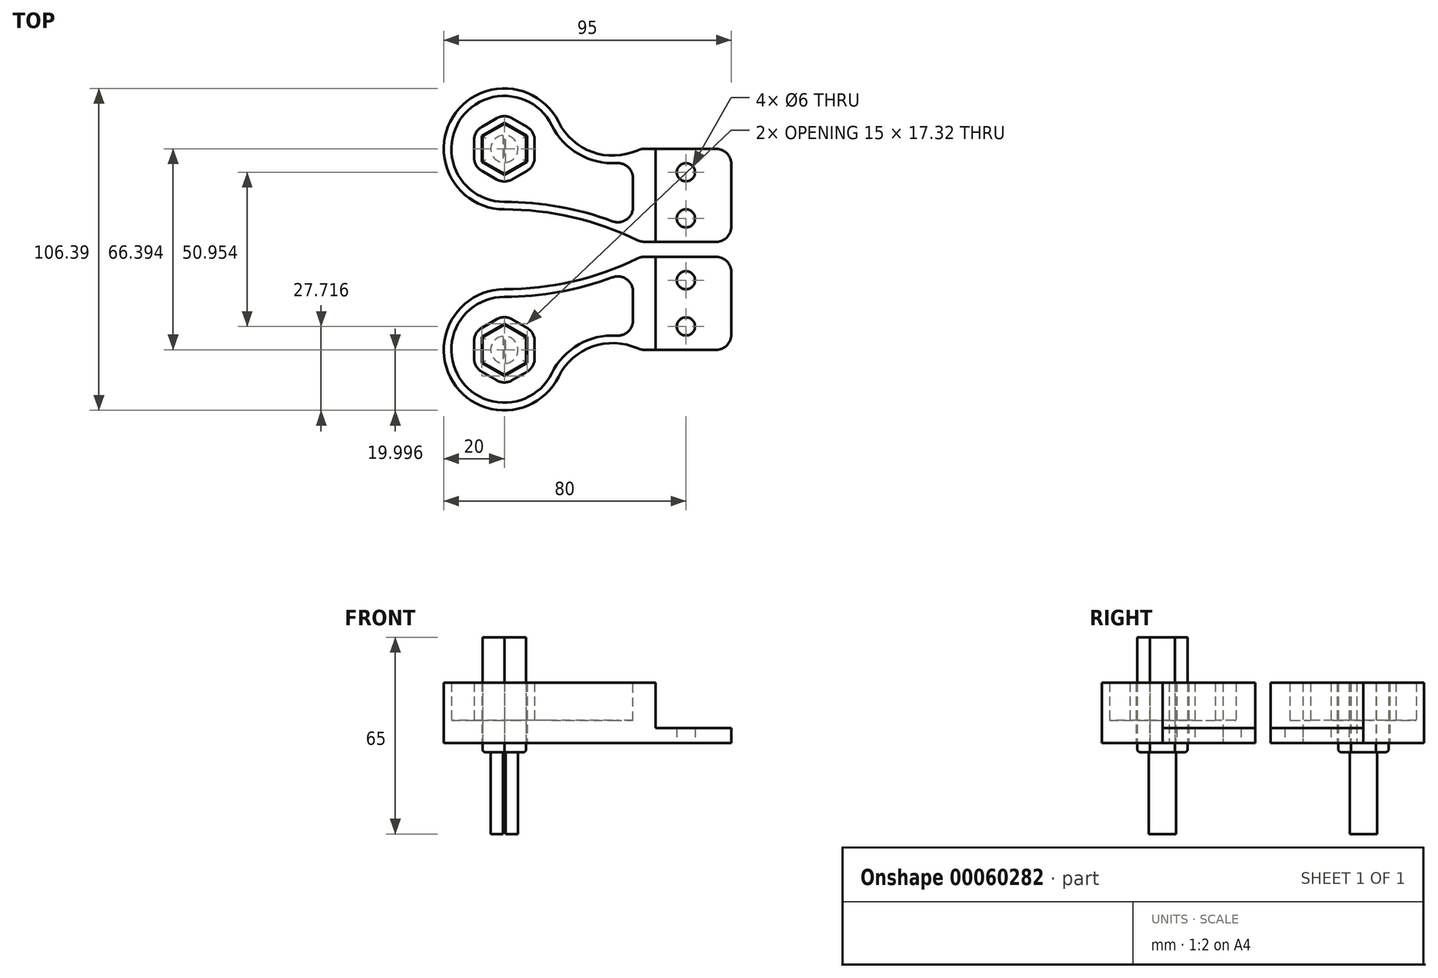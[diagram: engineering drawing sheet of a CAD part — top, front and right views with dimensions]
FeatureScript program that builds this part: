
annotation { "Feature Type Name" : "Feature", "Feature Type Description" : "" }
export const myFeature = defineFeature(function(context is Context, id is Id, definition is map)
    precondition{}
    {
        {
            var Q0;
            Q0=qCreatedBy(makeId("Top.planeOp"),FACE);
            var sketch = newSketch(context, id + "F0", { "sketchPlane" : qUnion([Q0])});
            skCircle(sketch, "E0", {"center": v(0, 0) * mm, "radius": 75 * mm, "construction": true});
            skLineSegment(sketch, "E1", {"start": v(0, 0) * mm, "end": v(75, 0) * mm, "construction": true});
            skCircle(sketch, "E2", {"center": v(0, 0) * mm, "radius": 20 * mm});
            skCircle(sketch, "E3", {"center": v(0, 0) * mm, "radius": 4.5 * mm});
            skCircle(sketch, "E4", {"center": v(0, 0) * mm, "radius": 1.5 * mm});
            skLineSegment(sketch, "E5", {"start": v(0, 0) * mm, "end": v(0, 4.5) * mm, "construction": true});
            skLineSegment(sketch, "E6", {"start": v(-0.5, 4.47) * mm, "end": v(-0.5, 1.41) * mm});
            skLineSegment(sketch, "E7", {"start": v(0.5, -4.47) * mm, "end": v(0.5, -1.41) * mm});
            skLineSegment(sketch, "E8.trimOffspring", {"start": v(-0.5, -1.41) * mm, "end": v(-0.5, -4.47) * mm});
            skLineSegment(sketch, "E9.trimOffspring", {"start": v(0.5, 1.41) * mm, "end": v(0.5, 4.47) * mm});
            skCircle(sketch, "E10.cCircle", {"center": v(0, 0) * mm, "radius": 7.5 * mm, "construction": true});
            skLineSegment(sketch, "E10.0", {"start": v(-7.5, -4.33) * mm, "end": v(-7.5, 4.33) * mm});
            skLineSegment(sketch, "E10.1", {"start": v(-7.5, 4.33) * mm, "end": v(0, 8.66) * mm});
            skLineSegment(sketch, "E10.2", {"start": v(0, 8.66) * mm, "end": v(7.5, 4.33) * mm});
            skLineSegment(sketch, "E10.3", {"start": v(7.5, 4.33) * mm, "end": v(7.5, -4.33) * mm});
            skLineSegment(sketch, "E10.4", {"start": v(7.5, -4.33) * mm, "end": v(0, -8.66) * mm});
            skLineSegment(sketch, "E10.5", {"start": v(0, -8.66) * mm, "end": v(-7.5, -4.33) * mm});
            skPoint(sketch, "E10.0.midPoint", {"position": v(-7.5, 0) * mm});
            skLineSegment(sketch, "E11.bottom", {"start": v(75, 0) * mm, "end": v(45, 0) * mm});
            skLineSegment(sketch, "E11.top", {"start": v(75, -30.7) * mm, "end": v(45, -30.7) * mm});
            skLineSegment(sketch, "E11.left", {"start": v(75, 0) * mm, "end": v(75, -30.7) * mm});
            skLineSegment(sketch, "E11.right", {"start": v(45, 0) * mm, "end": v(45, -30.7) * mm});
            skArc(sketch, "E12", {"start": v(45, -30.7) * mm, "mid": v(23.13, -22.71) * mm, "end": v(0, -20) * mm});
            skArc(sketch, "E13", {"start": v(17.92, 8.89) * mm, "mid": v(29.6, -1.23) * mm, "end": v(45, 0) * mm});
            skLineSegment(sketch, "E14", {"start": v(60, 0) * mm, "end": v(60, -7.72) * mm, "construction": true});
            skLineSegment(sketch, "E15", {"start": v(60, -22.98) * mm, "end": v(60, -30.7) * mm, "construction": true});
            skCircle(sketch, "E16", {"center": v(60, -7.72) * mm, "radius": 3 * mm});
            skCircle(sketch, "E17", {"center": v(60, -22.98) * mm, "radius": 3 * mm});
            skLineSegment(sketch, "E18.0", {"start": v(-7.2, -4.16) * mm, "end": v(-7.2, 4.16) * mm});
            skLineSegment(sketch, "E18.1", {"start": v(0, 8.31) * mm, "end": v(7.2, 4.16) * mm});
            skLineSegment(sketch, "E18.2", {"start": v(7.2, 4.16) * mm, "end": v(7.2, -4.16) * mm});
            skLineSegment(sketch, "E18.3", {"start": v(-7.2, 4.16) * mm, "end": v(0, 8.31) * mm});
            skLineSegment(sketch, "E18.4", {"start": v(7.2, -4.16) * mm, "end": v(0, -8.31) * mm});
            skLineSegment(sketch, "E18.5", {"start": v(0, -8.31) * mm, "end": v(-7.2, -4.16) * mm});
            skLineSegment(sketch, "E19", {"start": v(0.5, 1.41) * mm, "end": v(0.5, -1.41) * mm});
            skLineSegment(sketch, "E20", {"start": v(-0.5, 1.41) * mm, "end": v(-0.5, -1.41) * mm});
            skSolve(sketch);
        }
        {
            var Q0;
            Q0=makeQuery(id+"F0.imprint","IMPRINT",FACE,{"disambiguationData":[TD([[makeQuery(id+"F0.imprint","IMPRINT",EDGE,{"derivedFrom":sQuery(id+"F0.wireOp",EDGE,"E10.0")}),1.0]])]});
            var Q1;
            Q1=makeQuery(id+"F0.imprint","IMPRINT",FACE,{"disambiguationData":[TD([[makeQuery(id+"F0.imprint","IMPRINT",EDGE,{"derivedFrom":sQuery(id+"F0.wireOp",EDGE,"E11.right")}),-1.0]])]});
            var Q2;
            Q2=makeQuery(id+"F0.imprint","IMPRINT",FACE,{"disambiguationData":[TD([[makeQuery(id+"F0.imprint","IMPRINT",EDGE,{"derivedFrom":sQuery(id+"F0.wireOp",EDGE,"E11.bottom")}),1.0]])]});
            extrude(context, id + "F1", {"entities" : qUnion([Q0, Q1, Q2]), "depth" : 5 * mm});
        }
        {
            var Q0;
            Q0=makeQuery(id+"F1.opExtrude","CAP_FACE",FACE,{"disambiguationData":[OSD([sQuery(id+"F0.wireOp",EDGE,"E2"),sQuery(id+"F0.wireOp",EDGE,"E10.0"),sQuery(id+"F0.wireOp",EDGE,"E10.1"),sQuery(id+"F0.wireOp",EDGE,"E10.2"),sQuery(id+"F0.wireOp",EDGE,"E10.3"),sQuery(id+"F0.wireOp",EDGE,"E10.4"),sQuery(id+"F0.wireOp",EDGE,"E10.5"),sQuery(id+"F0.wireOp",EDGE,"E11.bottom"),sQuery(id+"F0.wireOp",EDGE,"E11.top"),sQuery(id+"F0.wireOp",EDGE,"E11.left"),sQuery(id+"F0.wireOp",EDGE,"E12"),sQuery(id+"F0.wireOp",EDGE,"E13")])],"isStart":false});
            var sketch = newSketch(context, id + "F2", { "sketchPlane" : qUnion([Q0])});
            skLineSegment(sketch, "E21.bottom", {"start": v(45, 0) * mm, "end": v(50, 0) * mm});
            skLineSegment(sketch, "E21.top", {"start": v(45, -30.7) * mm, "end": v(50, -30.7) * mm});
            skLineSegment(sketch, "E21.left", {"start": v(45, 0) * mm, "end": v(45, -30.7) * mm});
            skLineSegment(sketch, "E21.right", {"start": v(50, 0) * mm, "end": v(50, -30.7) * mm});
            skSolve(sketch);
        }
        {
            var Q0;
            Q0 = qSketchRegion(id + "F2", true);
            extrude(context, id + "F3", {"entities" : qUnion([Q0]), "operationType" : NewBodyOperationType.ADD, "depth" : 15 * mm});
        }
        {
            var Q0;
            {var subQ0=sQuery(id+"F0.wireOp",EDGE,"E11.bottom");var subQ1=sQuery(id+"F0.wireOp",EDGE,"E10.5");var subQ2=sQuery(id+"F0.wireOp",EDGE,"E10.4");var subQ3=sQuery(id+"F0.wireOp",EDGE,"E10.3");var subQ4=sQuery(id+"F0.wireOp",EDGE,"E2");var subQ5=sQuery(id+"F0.wireOp",EDGE,"E11.top");var subQ6=sQuery(id+"F0.wireOp",EDGE,"E10.0");var subQ7=sQuery(id+"F0.wireOp",EDGE,"E10.1");var subQ8=sQuery(id+"F0.wireOp",EDGE,"E12");var subQ9=sQuery(id+"F0.wireOp",EDGE,"E10.2");var subQ10=sQuery(id+"F0.wireOp",EDGE,"E13");Q0=makeQuery(id+"F3.boolean.opBoolean","SPLIT",FACE,{"disambiguationData":[TD([makeQuery(id+"F1.opExtrude","SWEPT_FACE",FACE,{"disambiguationData":[OSD([subQ4])]})])],"derivedFrom":makeQuery(id+"F1.opExtrude","CAP_FACE",FACE,{"disambiguationData":[OSD([subQ4,subQ6,subQ7,subQ9,subQ3,subQ2,subQ1,subQ0,subQ5,sQuery(id+"F0.wireOp",EDGE,"E11.left"),subQ8,subQ10])],"isStart":false})});}
            extrude(context, id + "F4", {"entities" : qUnion([Q0]), "depth" : 15 * mm});
        }
        {
            var Q0;
            Q0=makeQuery(id+"F4.opExtrude","CAP_FACE",FACE,{"disambiguationData":[OSD([sQuery(id+"F0.wireOp",EDGE,"E2"),sQuery(id+"F0.wireOp",EDGE,"E10.0"),sQuery(id+"F0.wireOp",EDGE,"E10.1"),sQuery(id+"F0.wireOp",EDGE,"E10.2"),sQuery(id+"F0.wireOp",EDGE,"E10.3"),sQuery(id+"F0.wireOp",EDGE,"E10.4"),sQuery(id+"F0.wireOp",EDGE,"E10.5"),sQuery(id+"F0.wireOp",EDGE,"E11.bottom"),sQuery(id+"F0.wireOp",EDGE,"E11.top"),sQuery(id+"F0.wireOp",EDGE,"E11.left"),sQuery(id+"F0.wireOp",EDGE,"E12"),sQuery(id+"F0.wireOp",EDGE,"E13")])],"isStart":false});
            shell(context, id + "F5", {"entities" : qUnion([Q0]), "thickness" : 2.5 * mm});
        }
        {
            var Q0;
            Q0=makeQuery(id+"F1.opExtrude","SWEPT_BODY",BODY,{"disambiguationData":[OSD([sQuery(id+"F0.wireOp",EDGE,"E2"),sQuery(id+"F0.wireOp",EDGE,"E10.0"),sQuery(id+"F0.wireOp",EDGE,"E10.1"),sQuery(id+"F0.wireOp",EDGE,"E10.2"),sQuery(id+"F0.wireOp",EDGE,"E10.3"),sQuery(id+"F0.wireOp",EDGE,"E10.4"),sQuery(id+"F0.wireOp",EDGE,"E10.5"),sQuery(id+"F0.wireOp",EDGE,"E11.bottom"),sQuery(id+"F0.wireOp",EDGE,"E11.top"),sQuery(id+"F0.wireOp",EDGE,"E11.left"),sQuery(id+"F0.wireOp",EDGE,"E12"),sQuery(id+"F0.wireOp",EDGE,"E13")])]});
            var Q1;
            Q1=makeQuery(id+"F4.opExtrude","SWEPT_BODY",BODY,{"disambiguationData":[OSD([sQuery(id+"F0.wireOp",EDGE,"E2"),sQuery(id+"F0.wireOp",EDGE,"E10.0"),sQuery(id+"F0.wireOp",EDGE,"E10.1"),sQuery(id+"F0.wireOp",EDGE,"E10.2"),sQuery(id+"F0.wireOp",EDGE,"E10.3"),sQuery(id+"F0.wireOp",EDGE,"E10.4"),sQuery(id+"F0.wireOp",EDGE,"E10.5"),sQuery(id+"F0.wireOp",EDGE,"E11.bottom"),sQuery(id+"F0.wireOp",EDGE,"E11.top"),sQuery(id+"F0.wireOp",EDGE,"E11.left"),sQuery(id+"F0.wireOp",EDGE,"E12"),sQuery(id+"F0.wireOp",EDGE,"E13")])]});
            booleanBodies(context, id + "F6", {"operationType" : BooleanOperationType.UNION, "tools" : qUnion([Q0, Q1])});
        }
        {
            var Q0;
            Q0=makeQuery(id+"F1.opExtrude","SWEPT_EDGE",EDGE,{"disambiguationData":[OSD([sQuery(id+"F0.wireOp",EDGE,"E11.bottom"),sQuery(id+"F0.wireOp",EDGE,"E11.left")])]});
            var Q1;
            Q1=makeQuery(id+"F1.opExtrude","SWEPT_EDGE",EDGE,{"disambiguationData":[OSD([sQuery(id+"F0.wireOp",EDGE,"E11.top"),sQuery(id+"F0.wireOp",EDGE,"E11.left")])]});
            var Q2;
            {var subQ0=sQuery(id+"F2.wireOp",EDGE,"E21.left");var subQ1=sQuery(id+"F2.wireOp",EDGE,"E21.top");var subQ2=sQuery(id+"F0.wireOp",EDGE,"E12");var subQ3=sQuery(id+"F0.wireOp",EDGE,"E11.right");var subQ4=sQuery(id+"F0.wireOp",EDGE,"E11.top");Q2=makeQuery(id+"F6.opBoolean","MERGE",EDGE,{"derivedFrom":[makeQuery(id+"F1.opExtrude","SWEPT_EDGE",EDGE,{"disambiguationData":[OSD([subQ4,subQ3,subQ2])]}),makeQuery(id+"F3.opExtrude","SWEPT_EDGE",EDGE,{"disambiguationData":[OSD([subQ2,subQ1,subQ0])]}),makeQuery(id+"F4.opExtrude","SWEPT_EDGE",EDGE,{"disambiguationData":[OSD([subQ4,subQ3,subQ2,subQ1,subQ0])]})]});}
            var Q3;
            {var subQ0=sQuery(id+"F2.wireOp",EDGE,"E21.left");var subQ1=sQuery(id+"F2.wireOp",EDGE,"E21.bottom");var subQ2=sQuery(id+"F0.wireOp",EDGE,"E13");var subQ3=sQuery(id+"F0.wireOp",EDGE,"E11.right");var subQ4=sQuery(id+"F0.wireOp",EDGE,"E11.bottom");Q3=makeQuery(id+"F6.opBoolean","MERGE",EDGE,{"derivedFrom":[makeQuery(id+"F1.opExtrude","SWEPT_EDGE",EDGE,{"disambiguationData":[OSD([subQ4,subQ3,subQ2])]}),makeQuery(id+"F3.opExtrude","SWEPT_EDGE",EDGE,{"disambiguationData":[OSD([subQ2,subQ1,subQ0])]}),makeQuery(id+"F4.opExtrude","SWEPT_EDGE",EDGE,{"disambiguationData":[OSD([subQ4,subQ3,subQ2,subQ1,subQ0])]})]});}
            var Q4;
            {var subQ0=sQuery(id+"F0.wireOp",EDGE,"E13");var subQ1=sQuery(id+"F0.wireOp",EDGE,"E2");Q4=makeQuery(id+"F6.opBoolean","MERGE",EDGE,{"derivedFrom":[makeQuery(id+"F1.opExtrude","SWEPT_EDGE",EDGE,{"disambiguationData":[OSD([subQ1,subQ0])]}),makeQuery(id+"F4.opExtrude","SWEPT_EDGE",EDGE,{"disambiguationData":[OSD([subQ1,subQ0])]})]});}
            var Q5;
            {var subQ0=sQuery(id+"F0.wireOp",EDGE,"E12");var subQ1=sQuery(id+"F0.wireOp",EDGE,"E2");Q5=makeQuery(id+"F6.opBoolean","MERGE",EDGE,{"derivedFrom":[makeQuery(id+"F1.opExtrude","SWEPT_EDGE",EDGE,{"disambiguationData":[OSD([subQ1,subQ0])]}),makeQuery(id+"F4.opExtrude","SWEPT_EDGE",EDGE,{"disambiguationData":[OSD([subQ1,subQ0])]})]});}
            var Q6;
            Q6=makeQuery(id+"F5.opShell","OFFSET_EDGE",EDGE,{"disambiguationData":[OSD([sQuery(id+"F0.wireOp",EDGE,"E11.bottom"),sQuery(id+"F0.wireOp",EDGE,"E11.right"),sQuery(id+"F0.wireOp",EDGE,"E13"),sQuery(id+"F2.wireOp",EDGE,"E21.bottom"),sQuery(id+"F2.wireOp",EDGE,"E21.left")])]});
            var Q7;
            Q7=makeQuery(id+"F5.opShell","OFFSET_EDGE",EDGE,{"disambiguationData":[OSD([sQuery(id+"F0.wireOp",EDGE,"E11.top"),sQuery(id+"F0.wireOp",EDGE,"E11.right"),sQuery(id+"F0.wireOp",EDGE,"E12"),sQuery(id+"F2.wireOp",EDGE,"E21.top"),sQuery(id+"F2.wireOp",EDGE,"E21.left")])]});
            var Q8;
            Q8=makeQuery(id+"F5.opShell","OFFSET_EDGE",EDGE,{"disambiguationData":[OSD([sQuery(id+"F0.wireOp",EDGE,"E10.4"),sQuery(id+"F0.wireOp",EDGE,"E10.5")])]});
            var Q9;
            Q9=makeQuery(id+"F5.opShell","OFFSET_EDGE",EDGE,{"disambiguationData":[OSD([sQuery(id+"F0.wireOp",EDGE,"E10.3"),sQuery(id+"F0.wireOp",EDGE,"E10.4")])]});
            var Q10;
            Q10=makeQuery(id+"F5.opShell","OFFSET_EDGE",EDGE,{"disambiguationData":[OSD([sQuery(id+"F0.wireOp",EDGE,"E10.0"),sQuery(id+"F0.wireOp",EDGE,"E10.5")])]});
            var Q11;
            Q11=makeQuery(id+"F5.opShell","OFFSET_EDGE",EDGE,{"disambiguationData":[OSD([sQuery(id+"F0.wireOp",EDGE,"E10.0"),sQuery(id+"F0.wireOp",EDGE,"E10.1")])]});
            var Q12;
            Q12=makeQuery(id+"F5.opShell","OFFSET_EDGE",EDGE,{"disambiguationData":[OSD([sQuery(id+"F0.wireOp",EDGE,"E10.1"),sQuery(id+"F0.wireOp",EDGE,"E10.2")])]});
            var Q13;
            Q13=makeQuery(id+"F5.opShell","OFFSET_EDGE",EDGE,{"disambiguationData":[OSD([sQuery(id+"F0.wireOp",EDGE,"E10.2"),sQuery(id+"F0.wireOp",EDGE,"E10.3")])]});
            fillet(context, id + "F7", {"entities" : qUnion([Q0, Q1, Q2, Q3, Q4, Q5, Q6, Q7, Q8, Q9, Q10, Q11, Q12, Q13]), "radius" : 5 * mm, "tangentPropagation" : true, "allowEdgeOverflow" : false});
        }
        {
            var Q0;
            Q0=makeQuery(id+"F0.imprint","IMPRINT",FACE,{"disambiguationData":[TD([[makeQuery(id+"F0.imprint","IMPRINT",EDGE,{"derivedFrom":sQuery(id+"F0.wireOp",EDGE,"E18.0")}),-1.0]])]});
            var Q1;
            {var subQ0=sQuery(id+"F0.wireOp",EDGE,"E6");Q1=makeQuery(id+"F0.imprint","IMPRINT",FACE,{"disambiguationData":[TD([[makeQuery(id+"F0.imprint","IMPRINT",EDGE,{"derivedFrom":subQ0}),-1.0]])]});}
            var Q2;
            {var subQ0=sQuery(id+"F0.wireOp",EDGE,"E7");Q2=makeQuery(id+"F0.imprint","IMPRINT",FACE,{"disambiguationData":[TD([[makeQuery(id+"F0.imprint","IMPRINT",EDGE,{"derivedFrom":subQ0}),-1.0]])]});}
            var Q3;
            {var subQ0=sQuery(id+"F0.wireOp",EDGE,"E4");var subQ1=makeQuery(id+"F0.imprint","INTERSECT",VERTEX,{"derivedFrom":[subQ0,sQuery(id+"F0.wireOp",EDGE,"E6")]});Q3=makeQuery(id+"F0.imprint","IMPRINT",FACE,{"disambiguationData":[TD([[makeQuery(id+"F0.imprint","IMPRINT",EDGE,{"disambiguationData":[TD([[subQ1,1.0]])],"derivedFrom":subQ0}),1.0]])]});}
            var Q4;
            {var subQ0=sQuery(id+"F0.wireOp",EDGE,"E7");Q4=makeQuery(id+"F0.imprint","IMPRINT",FACE,{"disambiguationData":[TD([[makeQuery(id+"F0.imprint","IMPRINT",EDGE,{"derivedFrom":subQ0}),1.0]])]});}
            var Q5;
            {var subQ0=sQuery(id+"F0.wireOp",EDGE,"E6");Q5=makeQuery(id+"F0.imprint","IMPRINT",FACE,{"disambiguationData":[TD([[makeQuery(id+"F0.imprint","IMPRINT",EDGE,{"derivedFrom":subQ0}),1.0]])]});}
            var Q6;
            {var subQ0=sQuery(id+"F0.wireOp",EDGE,"E19");Q6=makeQuery(id+"F0.imprint","IMPRINT",FACE,{"disambiguationData":[TD([[makeQuery(id+"F0.imprint","IMPRINT",EDGE,{"derivedFrom":subQ0}),1.0]])]});}
            var Q7;
            {var subQ0=sQuery(id+"F0.wireOp",EDGE,"E20");Q7=makeQuery(id+"F0.imprint","IMPRINT",FACE,{"disambiguationData":[TD([[makeQuery(id+"F0.imprint","IMPRINT",EDGE,{"derivedFrom":subQ0}),-1.0]])]});}
            var Q8;
            Q8=makeQuery(id+"F4.opExtrude","CAP_FACE",FACE,{"disambiguationData":[OSD([sQuery(id+"F0.wireOp",EDGE,"E2"),sQuery(id+"F0.wireOp",EDGE,"E10.0"),sQuery(id+"F0.wireOp",EDGE,"E10.1"),sQuery(id+"F0.wireOp",EDGE,"E10.2"),sQuery(id+"F0.wireOp",EDGE,"E10.3"),sQuery(id+"F0.wireOp",EDGE,"E10.4"),sQuery(id+"F0.wireOp",EDGE,"E10.5"),sQuery(id+"F0.wireOp",EDGE,"E11.bottom"),sQuery(id+"F0.wireOp",EDGE,"E11.top"),sQuery(id+"F0.wireOp",EDGE,"E11.left"),sQuery(id+"F0.wireOp",EDGE,"E12"),sQuery(id+"F0.wireOp",EDGE,"E13"),sQuery(id+"F0.wireOp",EDGE,"E16"),sQuery(id+"F0.wireOp",EDGE,"E17")])],"isStart":false});
            extrude(context, id + "F8", {"entities" : qUnion([Q0, Q1, Q2, Q3, Q4, Q5, Q6, Q7]), "endBound" : BoundingType.UP_TO_SURFACE, "endBoundEntityFace" : qUnion([Q8]), "depth" : 25 * mm, "hasSecondDirection" : true, "secondDirectionOppositeDirection" : true, "secondDirectionDepth" : 3 * mm});
        }
        {
            var Q0;
            {var subQ0=sQuery(id+"F0.wireOp",EDGE,"E6");Q0=makeQuery(id+"F0.imprint","IMPRINT",FACE,{"disambiguationData":[TD([[makeQuery(id+"F0.imprint","IMPRINT",EDGE,{"derivedFrom":subQ0}),-1.0]])]});}
            var Q1;
            {var subQ0=sQuery(id+"F0.wireOp",EDGE,"E7");Q1=makeQuery(id+"F0.imprint","IMPRINT",FACE,{"disambiguationData":[TD([[makeQuery(id+"F0.imprint","IMPRINT",EDGE,{"derivedFrom":subQ0}),-1.0]])]});}
            var Q2;
            {var subQ0=sQuery(id+"F0.wireOp",EDGE,"E19");Q2=makeQuery(id+"F0.imprint","IMPRINT",FACE,{"disambiguationData":[TD([[makeQuery(id+"F0.imprint","IMPRINT",EDGE,{"derivedFrom":subQ0}),1.0]])]});}
            var Q3;
            {var subQ0=sQuery(id+"F0.wireOp",EDGE,"E20");Q3=makeQuery(id+"F0.imprint","IMPRINT",FACE,{"disambiguationData":[TD([[makeQuery(id+"F0.imprint","IMPRINT",EDGE,{"derivedFrom":subQ0}),-1.0]])]});}
            extrude(context, id + "F9", {"entities" : qUnion([Q0, Q1, Q2, Q3]), "operationType" : NewBodyOperationType.ADD, "oppositeDirection" : true, "depth" : 30 * mm});
        }
        {
            var Q0;
            Q0=makeQuery(id+"F8.opExtrude","CAP_EDGE",EDGE,{"disambiguationData":[OSD([sQuery(id+"F0.wireOp",EDGE,"E18.3")])],"isStart":true});
            var Q1;
            Q1=makeQuery(id+"F8.opExtrude","CAP_EDGE",EDGE,{"disambiguationData":[OSD([sQuery(id+"F0.wireOp",EDGE,"E18.1")])],"isStart":true});
            var Q2;
            Q2=makeQuery(id+"F8.opExtrude","CAP_EDGE",EDGE,{"disambiguationData":[OSD([sQuery(id+"F0.wireOp",EDGE,"E18.2")])],"isStart":true});
            var Q3;
            Q3=makeQuery(id+"F8.opExtrude","CAP_EDGE",EDGE,{"disambiguationData":[OSD([sQuery(id+"F0.wireOp",EDGE,"E18.4")])],"isStart":true});
            var Q4;
            Q4=makeQuery(id+"F8.opExtrude","CAP_EDGE",EDGE,{"disambiguationData":[OSD([sQuery(id+"F0.wireOp",EDGE,"E18.0")])],"isStart":true});
            var Q5;
            Q5=makeQuery(id+"F8.opExtrude","CAP_EDGE",EDGE,{"disambiguationData":[OSD([sQuery(id+"F0.wireOp",EDGE,"E18.5")])],"isStart":true});
            fillet(context, id + "F10", {"entities" : qUnion([Q0, Q1, Q2, Q3, Q4, Q5]), "radius" : 1 * mm, "tangentPropagation" : true, "allowEdgeOverflow" : false});
        }
        {
            var Q0;
            Q0=makeQuery(id+"F8.opExtrude","SWEPT_BODY",BODY,{"disambiguationData":[OSD([sQuery(id+"F0.wireOp",EDGE,"E18.0"),sQuery(id+"F0.wireOp",EDGE,"E18.1"),sQuery(id+"F0.wireOp",EDGE,"E18.2"),sQuery(id+"F0.wireOp",EDGE,"E18.3"),sQuery(id+"F0.wireOp",EDGE,"E18.4"),sQuery(id+"F0.wireOp",EDGE,"E18.5")])]});
            transform(context, id + "F11", {"entities" : qUnion([Q0]), "transformType" : TransformType.TRANSLATION_3D, "dx" : 0 * mm, "dy" : -59.65 * mm, "dz" : 0 * mm, "makeCopy" : true});
        }
        {
            var Q0;
            Q0=makeQuery(id+"F11.opPattern","COPY",FACE,{"derivedFrom":makeQuery(id+"F8.opExtrude","CAP_FACE",FACE,{"disambiguationData":[OSD([sQuery(id+"F0.wireOp",EDGE,"E18.0"),sQuery(id+"F0.wireOp",EDGE,"E18.1"),sQuery(id+"F0.wireOp",EDGE,"E18.2"),sQuery(id+"F0.wireOp",EDGE,"E18.3"),sQuery(id+"F0.wireOp",EDGE,"E18.4"),sQuery(id+"F0.wireOp",EDGE,"E18.5")])],"isStart":false}),"instanceName":"1"});
            extrude(context, id + "F12", {"entities" : qUnion([Q0]), "operationType" : NewBodyOperationType.ADD, "depth" : 15 * mm});
        }
        {
            var Q0;
            Q0=makeQuery(id+"F1.opExtrude","SWEPT_BODY",BODY,{"disambiguationData":[OSD([sQuery(id+"F0.wireOp",EDGE,"E2"),sQuery(id+"F0.wireOp",EDGE,"E10.0"),sQuery(id+"F0.wireOp",EDGE,"E10.1"),sQuery(id+"F0.wireOp",EDGE,"E10.2"),sQuery(id+"F0.wireOp",EDGE,"E10.3"),sQuery(id+"F0.wireOp",EDGE,"E10.4"),sQuery(id+"F0.wireOp",EDGE,"E10.5"),sQuery(id+"F0.wireOp",EDGE,"E11.bottom"),sQuery(id+"F0.wireOp",EDGE,"E11.top"),sQuery(id+"F0.wireOp",EDGE,"E11.left"),sQuery(id+"F0.wireOp",EDGE,"E12"),sQuery(id+"F0.wireOp",EDGE,"E13"),sQuery(id+"F0.wireOp",EDGE,"E16"),sQuery(id+"F0.wireOp",EDGE,"E17")])]});
            var Q1;
            Q1=makeQuery(id+"F3.boolean.opBoolean","MERGE",FACE,{"derivedFrom":[makeQuery(id+"F1.opExtrude","SWEPT_FACE",FACE,{"disambiguationData":[OSD([sQuery(id+"F0.wireOp",EDGE,"E11.top")])]}),makeQuery(id+"F3.opExtrude","SWEPT_FACE",FACE,{"disambiguationData":[OSD([sQuery(id+"F2.wireOp",EDGE,"E21.top")])]})]});
            mirror(context, id + "F13", {"entities" : qUnion([Q0]), "mirrorPlane" : qUnion([Q1])});
        }
        {
            var Q0;
            Q0=makeQuery(id+"F13.opPattern","COPY",BODY,{"derivedFrom":makeQuery(id+"F1.opExtrude","SWEPT_BODY",BODY,{"disambiguationData":[OSD([sQuery(id+"F0.wireOp",EDGE,"E2"),sQuery(id+"F0.wireOp",EDGE,"E10.0"),sQuery(id+"F0.wireOp",EDGE,"E10.1"),sQuery(id+"F0.wireOp",EDGE,"E10.2"),sQuery(id+"F0.wireOp",EDGE,"E10.3"),sQuery(id+"F0.wireOp",EDGE,"E10.4"),sQuery(id+"F0.wireOp",EDGE,"E10.5"),sQuery(id+"F0.wireOp",EDGE,"E11.bottom"),sQuery(id+"F0.wireOp",EDGE,"E11.top"),sQuery(id+"F0.wireOp",EDGE,"E11.left"),sQuery(id+"F0.wireOp",EDGE,"E12"),sQuery(id+"F0.wireOp",EDGE,"E13"),sQuery(id+"F0.wireOp",EDGE,"E16"),sQuery(id+"F0.wireOp",EDGE,"E17")])]}),"instanceName":"1"});
            transform(context, id + "F14", {"entities" : qUnion([Q0]), "transformType" : TransformType.TRANSLATION_3D, "dx" : 0 * mm, "dy" : -5 * mm, "dz" : 0 * mm, "makeCopy" : false});
        }
        {
            var Q0;
            Q0=makeQuery(id+"F11.opPattern","COPY",BODY,{"derivedFrom":makeQuery(id+"F8.opExtrude","SWEPT_BODY",BODY,{"disambiguationData":[OSD([sQuery(id+"F0.wireOp",EDGE,"E18.0"),sQuery(id+"F0.wireOp",EDGE,"E18.1"),sQuery(id+"F0.wireOp",EDGE,"E18.2"),sQuery(id+"F0.wireOp",EDGE,"E18.3"),sQuery(id+"F0.wireOp",EDGE,"E18.4"),sQuery(id+"F0.wireOp",EDGE,"E18.5")])]}),"instanceName":"1"});
            var Q1;
            Q1=makeQuery(id+"F13.opPattern","COPY",EDGE,{"derivedFrom":makeQuery(id+"F1.opExtrude","CAP_EDGE",EDGE,{"disambiguationData":[OSD([sQuery(id+"F0.wireOp",EDGE,"E10.0")])],"isStart":true}),"instanceName":"1"});
            var Q2;
            Q2=makeQuery(id+"F13.opPattern","COPY",EDGE,{"derivedFrom":makeQuery(id+"F1.opExtrude","CAP_EDGE",EDGE,{"disambiguationData":[OSD([sQuery(id+"F0.wireOp",EDGE,"E10.0")])],"isStart":true}),"instanceName":"1"});
            transform(context, id + "F15", {"entities" : qUnion([Q0]), "transformType" : TransformType.TRANSLATION_DISTANCE, "transformDirection" : qUnion([Q2]), "distance" : 6.75 * mm, "makeCopy" : false});
        }
    });
